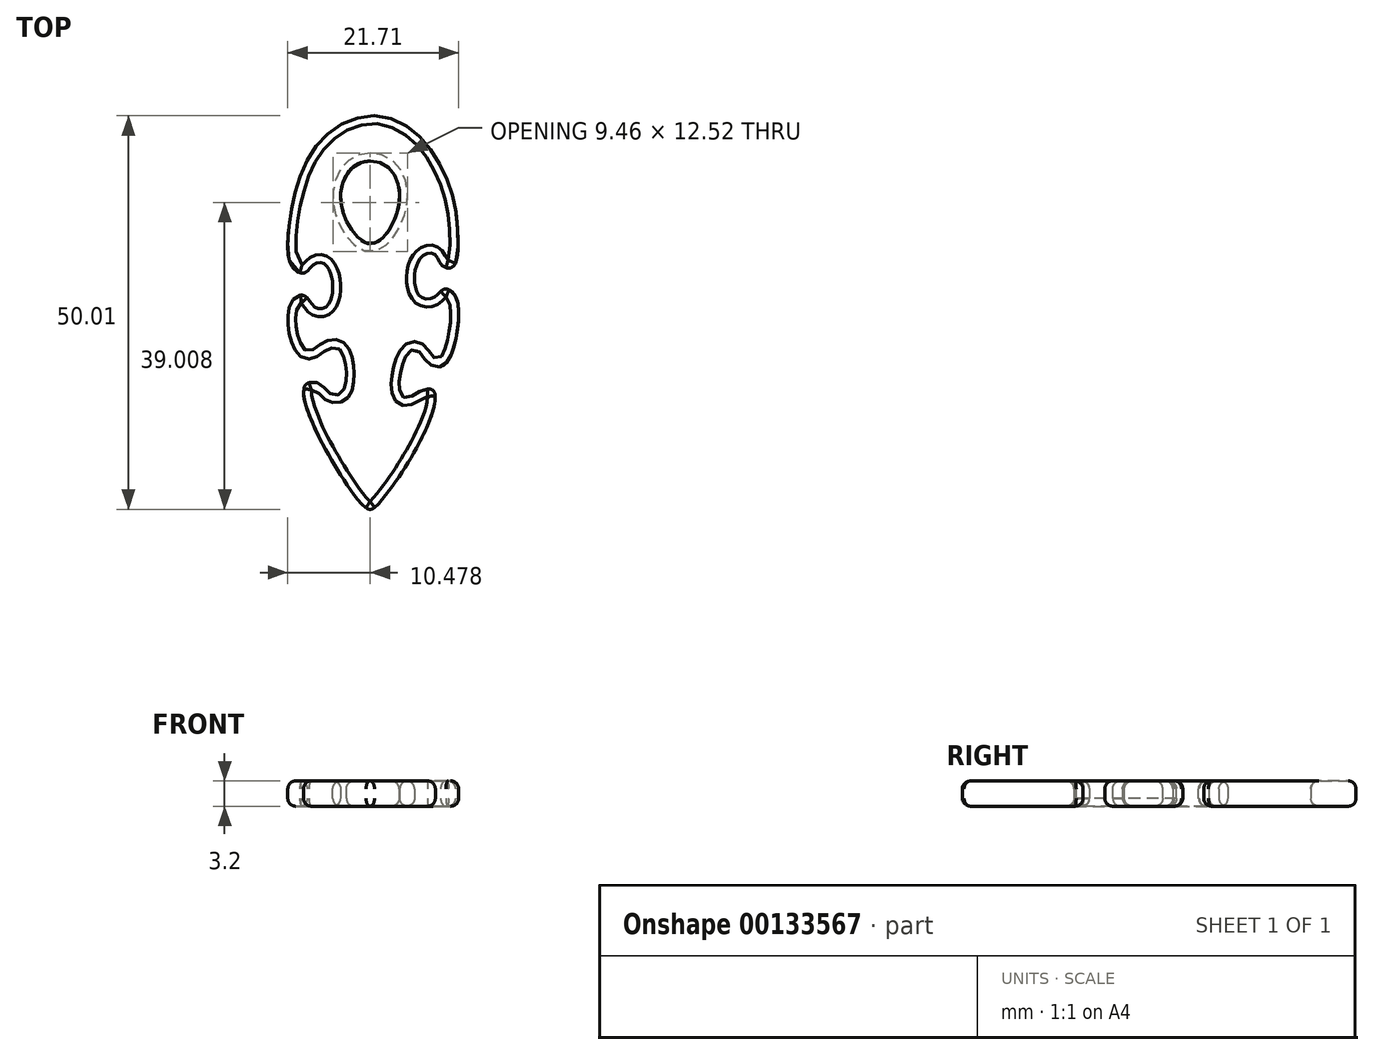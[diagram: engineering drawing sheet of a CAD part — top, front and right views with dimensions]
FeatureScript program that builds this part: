
annotation { "Feature Type Name" : "Feature", "Feature Type Description" : "" }
export const myFeature = defineFeature(function(context is Context, id is Id, definition is map)
    precondition{}
    {
        {
            var Q0;
            Q0=qCreatedBy(makeId("Top.planeOp"),FACE);
            var sketch = newSketch(context, id + "F0", { "sketchPlane" : qUnion([Q0])});
            skPoint(sketch, "E0.0.internal.snap0", {"position": v(0, 18.68) * mm});
            skFitSpline(sketch, "E1", {"points": [v(-0.01, 24.41) * mm, v(-6.37, 21.2) * mm, v(-9.56, 14.58) * mm, v(-10.5, 8.36) * mm, v(-9.87, 5.16) * mm, v(-8.4, 4.46) * mm, v(-7.15, 5.55) * mm, v(-5.51, 5.31) * mm, v(-5.2, 0.64) * mm, v(-6.91, 0) * mm, v(-8.22, 1.45) * mm, v(-9.52, 1.37) * mm, v(-10.5, -1.23) * mm, v(-8.94, -6.14) * mm, v(-7, -6.3) * mm, v(-5.8, -5.48) * mm, v(-3.94, -5.25) * mm, v(-3.47, -10.54) * mm, v(-5.04, -10.9) * mm, v(-6.51, -9.6) * mm, v(-8.3, -9.84) * mm, v(-7.37, -14.6) * mm, v(-4.56, -19.97) * mm, v(-1.64, -24.33) * mm, v(0, -25.59) * mm, v(1.43, -24.42) * mm, v(3.86, -21.08) * mm, v(7.46, -14.42) * mm, v(8.05, -10.58) * mm, v(6.66, -10.39) * mm, v(4.94, -11.32) * mm, v(3.85, -11.01) * mm, v(4.47, -6.18) * mm, v(5.78, -5.28) * mm, v(6.82, -6.38) * mm, v(7.7, -7.25) * mm, v(9.25, -7.32) * mm, v(11.05, -2.72) * mm, v(10.62, 1.8) * mm, v(9.3, 2.35) * mm, v(8.14, 1.38) * mm, v(6.34, 1.45) * mm, v(5.64, 4.5) * mm, v(6.81, 6.75) * mm, v(8.14, 6.83) * mm, v(9.15, 5.35) * mm, v(10.54, 5.31) * mm, v(11.06, 9.93) * mm, v(10.2, 14.99) * mm, v(6.2, 21.8) * mm, v(-0.01, 24.41) * mm]});
            skFitSpline(sketch, "E2", {"points": [v(0, 18.68) * mm, v(-2.35, 17.78) * mm, v(-3.71, 13.26) * mm, v(0, 8.16) * mm, v(3.65, 13.26) * mm, v(2.36, 17.78) * mm, v(0, 18.68) * mm]});
            skSolve(sketch);
        }
        {
            var Q0;
            Q0=makeQuery(id+"F0.imprint","IMPRINT",FACE,{"disambiguationData":[TD([[makeQuery(id+"F0.imprint","IMPRINT",EDGE,{"derivedFrom":sQuery(id+"F0.wireOp",EDGE,"E1")}),1.0]])]});
            extrude(context, id + "F1", {"entities" : qUnion([Q0]), "depth" : 3.2 * mm});
        }
        {
            var Q0;
            Q0=makeQuery(id+"F1.opExtrude","CAP_FACE",FACE,{"disambiguationData":[OSD([sQuery(id+"F0.wireOp",EDGE,"E1"),sQuery(id+"F0.wireOp",EDGE,"E2")])],"isStart":true});
            var Q1;
            Q1=makeQuery(id+"F1.opExtrude","CAP_FACE",FACE,{"disambiguationData":[OSD([sQuery(id+"F0.wireOp",EDGE,"E1"),sQuery(id+"F0.wireOp",EDGE,"E2")])],"isStart":false});
            fillet(context, id + "F2", {"entities" : qUnion([Q0, Q1]), "radius" : 1 * mm, "tangentPropagation" : true, "allowEdgeOverflow" : false});
        }
    });
